# Revit family: HD002-2015.01.12-BT-Conjunto Celosia 70S
name_source: partatom
category: Generic Models
revit_build: Autodesk Revit 2016 (Build: 20150714_1515(x64)
units: mm (PartAtom-declared; Revit-internal decimal feet)

## family parameters
Always vertical = Yes
Can host rebar = No
Cut with Voids When Loaded = No
Part Type = Normal
Room Calculation Point = No
Round Connector Dimension = Use Diameter
Shared = No
Work Plane-Based = No

## types (1)
- Productos HD
    BT_Alto = 2500 mm  [stored 8.2021 ft]
    BT_Ancho = 2000 mm  [stored 6.56168 ft]
    BT_Codigo_Linea = De Línea
    BT_Codigo_Origen = HD010
    BT_Color = 100 colores a eleccion
    BT_EETT = Producto diseñado para ser utilizado en espacios en los que se requiera renovación de aire o simplemente como elemento decorativo, además del control solar pasivo.
    BT_Elemento = Celosias y Quiebravista
    BT_Especialidad = Arquitectura
    BT_Itemizado_Estandar_CDT = D 01 08 03
    BT_Marca = Hunter Douglas
    BT_MasterFormat® = 08 91 19
    BT_Material = Aluzinc
    BT_Nombre_Corto = Celosia 70S
    BT_Nombre_Tecnico = Celosia 70S Horizontal
    BT_Profundidad = 135 mm  [stored 0.442913 ft]
    BT_SKU = 003023
    BT_Uso = Exterior
    Cantidad  Paneles = 34
    Cantidad  Portapaneles = 3
    Cantidad Anclajes Soporte = 5
    Description = Celisía 70S tiene función decorativa, renovación de aire o control solar pasivo.
    Distancia  entre apoyos = 1800 mm  [stored 5.90551 ft]
    ID_Objeto = BT_F_F_010
    ID_Source = BIMTOOL
    Manufacturer = Hunter Douglas
    URL = http://www.hunterdouglas.cl

note: [stored X ft] marks values corroborated as IEEE doubles in the binary element streams (Revit-internal decimal feet)

## geometry (parser evidence)
native form markers: Sweep x15
no freeform markers — native parametric forms only
